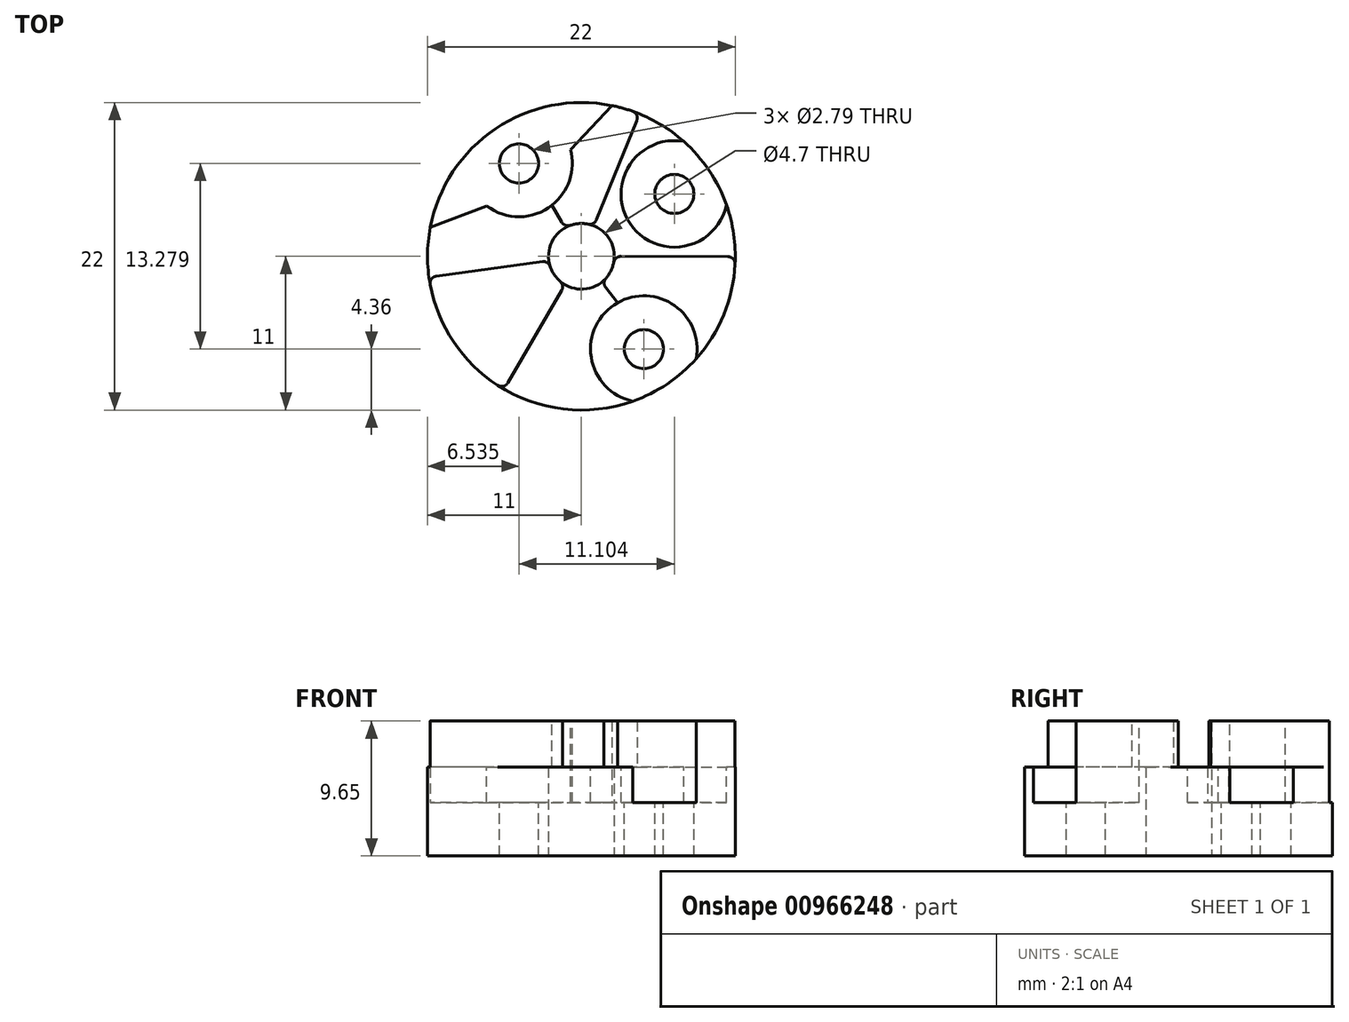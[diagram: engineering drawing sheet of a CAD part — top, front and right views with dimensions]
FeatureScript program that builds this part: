
annotation { "Feature Type Name" : "Feature", "Feature Type Description" : "" }
export const myFeature = defineFeature(function(context is Context, id is Id, definition is map)
    precondition{}
    {
        {
            var Q0;
            Q0=qCreatedBy(makeId("Top.planeOp"),FACE);
            var sketch = newSketch(context, id + "F0", { "sketchPlane" : qUnion([Q0])});
            skCircle(sketch, "E0", {"center": v(0, 0) * mm, "radius": 11 * mm});
            skCircle(sketch, "E1", {"center": v(0, 0) * mm, "radius": 2.35 * mm});
            skLineSegment(sketch, "E2", {"start": v(0, 0) * mm, "end": v(4.15, 10.19) * mm});
            skLineSegment(sketch, "E3", {"start": v(0, 0) * mm, "end": v(-5.47, 9.54) * mm});
            skLineSegment(sketch, "E4.1.0", {"start": v(0, 0) * mm, "end": v(11, -0.03) * mm});
            skLineSegment(sketch, "E4.1.1", {"start": v(0, 0) * mm, "end": v(6.75, -8.69) * mm});
            skLineSegment(sketch, "E4.2.0", {"start": v(0, 0) * mm, "end": v(-5.53, -9.5) * mm});
            skLineSegment(sketch, "E4.2.1", {"start": v(0, 0) * mm, "end": v(-10.9, -1.5) * mm});
            skLineSegment(sketch, "E4.anchor1", {"start": v(0, 0) * mm, "end": v(-5.47, 9.54) * mm, "construction": true});
            skLineSegment(sketch, "E4.anchor2", {"start": v(0, 0) * mm, "end": v(-5.53, -9.5) * mm, "construction": true});
            skSolve(sketch);
        }
        {
            var Q0;
            {var subQ0=sQuery(id+"F0.wireOp",EDGE,"E2");var subQ1=sQuery(id+"F0.wireOp",EDGE,"E0");var subQ2=makeQuery(id+"F0.imprint","INTERSECT",VERTEX,{"derivedFrom":[subQ1,subQ0]});Q0=makeQuery(id+"F0.imprint","IMPRINT",FACE,{"disambiguationData":[TD([[makeQuery(id+"F0.imprint","IMPRINT",EDGE,{"disambiguationData":[TD([[subQ2,-1.0]])],"derivedFrom":subQ1}),1.0]])]});}
            var Q1;
            {var subQ0=sQuery(id+"F0.wireOp",EDGE,"E4.2.0");var subQ1=sQuery(id+"F0.wireOp",EDGE,"E0");var subQ2=makeQuery(id+"F0.imprint","INTERSECT",VERTEX,{"derivedFrom":[subQ1,subQ0]});Q1=makeQuery(id+"F0.imprint","IMPRINT",FACE,{"disambiguationData":[TD([[makeQuery(id+"F0.imprint","IMPRINT",EDGE,{"disambiguationData":[TD([[subQ2,1.0]])],"derivedFrom":subQ1}),1.0]])]});}
            var Q2;
            {var subQ0=sQuery(id+"F0.wireOp",EDGE,"E4.1.0");var subQ1=sQuery(id+"F0.wireOp",EDGE,"E0");var subQ2=makeQuery(id+"F0.imprint","INTERSECT",VERTEX,{"derivedFrom":[subQ1,subQ0]});Q2=makeQuery(id+"F0.imprint","IMPRINT",FACE,{"disambiguationData":[TD([[makeQuery(id+"F0.imprint","IMPRINT",EDGE,{"disambiguationData":[TD([[subQ2,1.0]])],"derivedFrom":subQ1}),1.0]])]});}
            extrude(context, id + "F1", {"entities" : qUnion([Q0, Q1, Q2]), "depth" : 3.3 * mm});
        }
        {
            var Q0;
            {var subQ0=sQuery(id+"F0.wireOp",EDGE,"33BuIZ9v-IkX0-KjEr-VNsg-VApjckLjgjfI");var subQ1=sQuery(id+"F0.wireOp",EDGE,"E0");var subQ2=makeQuery(id+"F0.imprint","INTERSECT",VERTEX,{"derivedFrom":[subQ1,subQ0]});Q0=makeQuery(id+"F0.imprint","IMPRINT",FACE,{"disambiguationData":[TD([[makeQuery(id+"F0.imprint","IMPRINT",EDGE,{"disambiguationData":[TD([[subQ2,1.0]])],"derivedFrom":subQ1}),1.0]])]});}
            var Q1;
            {var subQ0=sQuery(id+"F0.wireOp",EDGE,"dZoegOkE-iBWH-g3UK-yCjy-q1fHpqfjE5M4");var subQ1=sQuery(id+"F0.wireOp",EDGE,"E0");var subQ2=makeQuery(id+"F0.imprint","INTERSECT",VERTEX,{"derivedFrom":[subQ1,subQ0]});Q1=makeQuery(id+"F0.imprint","IMPRINT",FACE,{"disambiguationData":[TD([[makeQuery(id+"F0.imprint","IMPRINT",EDGE,{"disambiguationData":[TD([[subQ2,1.0]])],"derivedFrom":subQ1}),1.0]])]});}
            var Q2;
            {var subQ0=sQuery(id+"F0.wireOp",EDGE,"073fcc1c-5e5f-4306-95f4-ba863140295b.1.1");var subQ1=sQuery(id+"F0.wireOp",EDGE,"E0");var subQ2=makeQuery(id+"F0.imprint","INTERSECT",VERTEX,{"derivedFrom":[subQ1,subQ0]});Q2=makeQuery(id+"F0.imprint","IMPRINT",FACE,{"disambiguationData":[TD([[makeQuery(id+"F0.imprint","IMPRINT",EDGE,{"disambiguationData":[TD([[subQ2,1.0]])],"derivedFrom":subQ1}),1.0]])]});}
            var Q3;
            {var subQ0=sQuery(id+"F0.wireOp",EDGE,"073fcc1c-5e5f-4306-95f4-ba863140295b.1.0");var subQ1=sQuery(id+"F0.wireOp",EDGE,"E0");var subQ2=makeQuery(id+"F0.imprint","INTERSECT",VERTEX,{"derivedFrom":[subQ1,subQ0]});Q3=makeQuery(id+"F0.imprint","IMPRINT",FACE,{"disambiguationData":[TD([[makeQuery(id+"F0.imprint","IMPRINT",EDGE,{"disambiguationData":[TD([[subQ2,1.0]])],"derivedFrom":subQ1}),1.0]])]});}
            var Q4;
            {var subQ0=sQuery(id+"F0.wireOp",EDGE,"073fcc1c-5e5f-4306-95f4-ba863140295b.2.0");var subQ1=sQuery(id+"F0.wireOp",EDGE,"E0");var subQ2=makeQuery(id+"F0.imprint","INTERSECT",VERTEX,{"derivedFrom":[subQ1,subQ0]});Q4=makeQuery(id+"F0.imprint","IMPRINT",FACE,{"disambiguationData":[TD([[makeQuery(id+"F0.imprint","IMPRINT",EDGE,{"disambiguationData":[TD([[subQ2,1.0]])],"derivedFrom":subQ1}),1.0]])]});}
            var Q5;
            {var subQ0=sQuery(id+"F0.wireOp",EDGE,"33BuIZ9v-IkX0-KjEr-VNsg-VApjckLjgjfI");var subQ1=sQuery(id+"F0.wireOp",EDGE,"E0");var subQ2=makeQuery(id+"F0.imprint","INTERSECT",VERTEX,{"derivedFrom":[subQ1,subQ0]});Q5=makeQuery(id+"F0.imprint","IMPRINT",FACE,{"disambiguationData":[TD([[makeQuery(id+"F0.imprint","IMPRINT",EDGE,{"disambiguationData":[TD([[subQ2,-1.0]])],"derivedFrom":subQ1}),1.0]])]});}
            extrude(context, id + "F2", {"entities" : qUnion([Q0, Q1, Q2, Q3, Q4, Q5]), "operationType" : NewBodyOperationType.ADD, "oppositeDirection" : true, "depth" : 6.35 * mm});
        }
        {
            var Q0;
            Q0=makeQuery(id+"F1.opExtrude","SWEPT_EDGE",EDGE,{"disambiguationData":[OSD([sQuery(id+"F0.wireOp",EDGE,"E0"),sQuery(id+"F0.wireOp",EDGE,"E2")])]});
            var Q1;
            Q1=makeQuery(id+"F1.opExtrude","SWEPT_EDGE",EDGE,{"disambiguationData":[OSD([sQuery(id+"F0.wireOp",EDGE,"E0"),sQuery(id+"F0.wireOp",EDGE,"E4.1.0")])]});
            var Q2;
            Q2=makeQuery(id+"F1.opExtrude","SWEPT_EDGE",EDGE,{"disambiguationData":[OSD([sQuery(id+"F0.wireOp",EDGE,"E0"),sQuery(id+"F0.wireOp",EDGE,"E3")])]});
            var Q3;
            Q3=makeQuery(id+"F1.opExtrude","SWEPT_EDGE",EDGE,{"disambiguationData":[OSD([sQuery(id+"F0.wireOp",EDGE,"E0"),sQuery(id+"F0.wireOp",EDGE,"E4.1.1")])]});
            var Q4;
            Q4=makeQuery(id+"F1.opExtrude","SWEPT_EDGE",EDGE,{"disambiguationData":[OSD([sQuery(id+"F0.wireOp",EDGE,"E0"),sQuery(id+"F0.wireOp",EDGE,"E4.2.0")])]});
            var Q5;
            Q5=makeQuery(id+"F1.opExtrude","SWEPT_EDGE",EDGE,{"disambiguationData":[OSD([sQuery(id+"F0.wireOp",EDGE,"E0"),sQuery(id+"F0.wireOp",EDGE,"E4.2.1")])]});
            fillet(context, id + "F3", {"entities" : qUnion([Q0, Q1, Q2, Q3, Q4, Q5]), "radius" : 0.5 * mm, "tangentPropagation" : true, "allowEdgeOverflow" : false});
        }
        {
            var Q0;
            Q0=makeQuery(id+"F1.opExtrude","SWEPT_EDGE",EDGE,{"disambiguationData":[OSD([sQuery(id+"F0.wireOp",EDGE,"E1"),sQuery(id+"F0.wireOp",EDGE,"E4.2.1")])]});
            var Q1;
            Q1=makeQuery(id+"F1.opExtrude","SWEPT_EDGE",EDGE,{"disambiguationData":[OSD([sQuery(id+"F0.wireOp",EDGE,"E1"),sQuery(id+"F0.wireOp",EDGE,"E4.2.0")])]});
            var Q2;
            Q2=makeQuery(id+"F1.opExtrude","SWEPT_EDGE",EDGE,{"disambiguationData":[OSD([sQuery(id+"F0.wireOp",EDGE,"E1"),sQuery(id+"F0.wireOp",EDGE,"E3")])]});
            var Q3;
            Q3=makeQuery(id+"F1.opExtrude","SWEPT_EDGE",EDGE,{"disambiguationData":[OSD([sQuery(id+"F0.wireOp",EDGE,"E1"),sQuery(id+"F0.wireOp",EDGE,"E2")])]});
            var Q4;
            Q4=makeQuery(id+"F1.opExtrude","SWEPT_EDGE",EDGE,{"disambiguationData":[OSD([sQuery(id+"F0.wireOp",EDGE,"E1"),sQuery(id+"F0.wireOp",EDGE,"E4.1.1")])]});
            var Q5;
            Q5=makeQuery(id+"F1.opExtrude","SWEPT_EDGE",EDGE,{"disambiguationData":[OSD([sQuery(id+"F0.wireOp",EDGE,"E1"),sQuery(id+"F0.wireOp",EDGE,"E4.1.0")])]});
            fillet(context, id + "F4", {"entities" : qUnion([Q0, Q1, Q2, Q3, Q4, Q5]), "radius" : 0.5 * mm, "tangentPropagation" : true, "allowEdgeOverflow" : false});
        }
        {
            var Q0;
            {var subQ1=sQuery(id+"F0.wireOp",EDGE,"E0");var subQ4=sQuery(id+"F0.wireOp",EDGE,"E1");var subQ5=sQuery(id+"F0.wireOp",EDGE,"E2");Q0=makeQuery(id+"F2.boolean.opBoolean","SPLIT",FACE,{"disambiguationData":[TD([makeQuery(id+"F1.opExtrude","SWEPT_FACE",FACE,{"disambiguationData":[OSD([subQ5])]})])],"derivedFrom":makeQuery(id+"F2.opExtrude","CAP_FACE",FACE,{"disambiguationData":[OSD([subQ1,subQ4])],"isStart":true})});}
            var sketch = newSketch(context, id + "F5", { "sketchPlane" : qUnion([Q0])});
            skCircle(sketch, "E5", {"center": v(6.64, 4.46) * mm, "radius": 1.4 * mm});
            skCircle(sketch, "E6.1.0", {"center": v(-4.46, 6.64) * mm, "radius": 1.4 * mm});
            skCircle(sketch, "E6.2.0", {"center": v(-6.64, -4.46) * mm, "radius": 1.4 * mm});
            skCircle(sketch, "E6.3.0", {"center": v(4.46, -6.64) * mm, "radius": 1.4 * mm});
            skPoint(sketch, "E6.center", {"position": v(0, 0) * mm});
            skSolve(sketch);
        }
        {
            var Q0;
            Q0=makeQuery(id+"F5.imprint","IMPRINT",FACE,{"disambiguationData":[TD([[makeQuery(id+"F5.imprint","IMPRINT",EDGE,{"derivedFrom":sQuery(id+"F5.wireOp",EDGE,"E6.1.0")}),1.0]])]});
            var Q1;
            Q1=makeQuery(id+"F5.imprint","IMPRINT",FACE,{"disambiguationData":[TD([[makeQuery(id+"F5.imprint","IMPRINT",EDGE,{"derivedFrom":sQuery(id+"F5.wireOp",EDGE,"E5")}),1.0]])]});
            var Q2;
            Q2=makeQuery(id+"F5.imprint","IMPRINT",FACE,{"disambiguationData":[TD([[makeQuery(id+"F5.imprint","IMPRINT",EDGE,{"derivedFrom":sQuery(id+"F5.wireOp",EDGE,"E6.3.0")}),1.0]])]});
            extrude(context, id + "F6", {"entities" : qUnion([Q0, Q1, Q2]), "operationType" : NewBodyOperationType.REMOVE, "endBound" : BoundingType.THROUGH_ALL, "oppositeDirection" : true, "depth" : 25.4 * mm, "hasSecondDirection" : true, "secondDirectionOppositeDirection" : false, "secondDirectionDepth" : 25.4 * mm});
        }
        {
            var Q0;
            Q0=makeQuery(id+"F1.opExtrude","CAP_FACE",FACE,{"disambiguationData":[OSD([sQuery(id+"F0.wireOp",EDGE,"E0"),sQuery(id+"F0.wireOp",EDGE,"E1"),sQuery(id+"F0.wireOp",EDGE,"E2"),sQuery(id+"F0.wireOp",EDGE,"E3")])],"isStart":false});
            var sketch = newSketch(context, id + "F7", { "sketchPlane" : qUnion([Q0])});
            skCircle(sketch, "E7", {"center": v(-4.46, 6.64) * mm, "radius": 3.8 * mm});
            skCircle(sketch, "E8.1.0", {"center": v(-6.64, -4.46) * mm, "radius": 3.8 * mm});
            skCircle(sketch, "E8.2.0", {"center": v(4.46, -6.64) * mm, "radius": 3.8 * mm});
            skCircle(sketch, "E8.3.0", {"center": v(6.64, 4.46) * mm, "radius": 3.8 * mm});
            skPoint(sketch, "E8.center", {"position": v(0, 0) * mm});
            skSolve(sketch);
        }
        {
            var Q0;
            Q0=makeQuery(id+"F7.imprint","IMPRINT",FACE,{"disambiguationData":[TD([[makeQuery(id+"F7.imprint","IMPRINT",EDGE,{"derivedFrom":sQuery(id+"F7.wireOp",EDGE,"E8.2.0")}),1.0]])]});
            var Q1;
            Q1=makeQuery(id+"F7.imprint","IMPRINT",FACE,{"disambiguationData":[TD([[makeQuery(id+"F7.imprint","IMPRINT",EDGE,{"derivedFrom":sQuery(id+"F7.wireOp",EDGE,"E8.3.0")}),1.0]])]});
            var Q2;
            {var subQ0=sQuery(id+"F0.wireOp",EDGE,"E3");var subQ1=sQuery(id+"F0.wireOp",EDGE,"E2");var subQ2=sQuery(id+"F0.wireOp",EDGE,"E1");var subQ3=sQuery(id+"F0.wireOp",EDGE,"E0");var subQ4=makeQuery(id+"F1.opExtrude","CAP_FACE",FACE,{"disambiguationData":[OSD([subQ3,subQ2,subQ1,subQ0])],"isStart":false});var subQ5=makeQuery(id+"F6.opExtrude","SWEPT_FACE",FACE,{"disambiguationData":[OSD([sQuery(id+"F5.wireOp",EDGE,"E6.1.0")])]});var subQ8=makeQuery(id+"F6.boolean.opBoolean","INTERSECT",EDGE,{"derivedFrom":[subQ4,subQ5]});Q2=makeQuery(id+"F7.imprint","IMPRINT",FACE,{"disambiguationData":[TD([[makeQuery(id+"F7.imprint","IMPRINT",EDGE,{"derivedFrom":subQ8}),1.0]])]});}
            var Q3;
            {var subQ0=sQuery(id+"F0.wireOp",EDGE,"E3");var subQ1=sQuery(id+"F0.wireOp",EDGE,"E2");var subQ2=sQuery(id+"F0.wireOp",EDGE,"E1");var subQ3=sQuery(id+"F0.wireOp",EDGE,"E0");var subQ4=makeQuery(id+"F1.opExtrude","CAP_FACE",FACE,{"disambiguationData":[OSD([subQ3,subQ2,subQ1,subQ0])],"isStart":false});var subQ5=makeQuery(id+"F6.opExtrude","SWEPT_FACE",FACE,{"disambiguationData":[OSD([sQuery(id+"F5.wireOp",EDGE,"E6.1.0")])]});var subQ8=makeQuery(id+"F6.boolean.opBoolean","INTERSECT",EDGE,{"derivedFrom":[subQ4,subQ5]});Q3=makeQuery(id+"F7.imprint","IMPRINT",FACE,{"disambiguationData":[TD([[makeQuery(id+"F7.imprint","IMPRINT",EDGE,{"derivedFrom":subQ8}),-1.0]])]});}
            extrude(context, id + "F8", {"entities" : qUnion([Q0, Q1, Q2, Q3]), "operationType" : NewBodyOperationType.REMOVE, "oppositeDirection" : true, "depth" : 5.84 * mm});
        }
        {
            var Q0;
            {var subQ0=sQuery(id+"F0.wireOp",EDGE,"E0");Q0=makeQuery(id+"F8.boolean.opBoolean","INTERSECT",EDGE,{"disambiguationData":[OD(0.0)],"derivedFrom":[makeQuery(id+"F2.boolean.opBoolean","MERGE",FACE,{"derivedFrom":[makeQuery(id+"F1.opExtrude","SWEPT_FACE",FACE,{"disambiguationData":[OSD([subQ0]),TDD([makeQuery(id+"F0.imprint","IMPRINT",EDGE,{"disambiguationData":[TD([[makeQuery(id+"F0.imprint","INTERSECT",VERTEX,{"derivedFrom":[subQ0,sQuery(id+"F0.wireOp",EDGE,"E2")]}),-1.0]])],"derivedFrom":subQ0})])]}),makeQuery(id+"F1.opExtrude","SWEPT_FACE",FACE,{"disambiguationData":[OSD([subQ0]),TDD([makeQuery(id+"F0.imprint","IMPRINT",EDGE,{"disambiguationData":[TD([[makeQuery(id+"F0.imprint","INTERSECT",VERTEX,{"derivedFrom":[subQ0,sQuery(id+"F0.wireOp",EDGE,"E4.2.0")]}),1.0]])],"derivedFrom":subQ0})])]}),makeQuery(id+"F1.opExtrude","SWEPT_FACE",FACE,{"disambiguationData":[OSD([subQ0]),TDD([makeQuery(id+"F0.imprint","IMPRINT",EDGE,{"disambiguationData":[TD([[makeQuery(id+"F0.imprint","INTERSECT",VERTEX,{"derivedFrom":[subQ0,sQuery(id+"F0.wireOp",EDGE,"E4.1.0")]}),1.0]])],"derivedFrom":subQ0})])]}),makeQuery(id+"F2.opExtrude","SWEPT_FACE",FACE,{"disambiguationData":[OSD([subQ0])]})]}),makeQuery(id+"F8.opExtrude","SWEPT_FACE",FACE,{"disambiguationData":[OSD([sQuery(id+"F7.wireOp",EDGE,"E7")])]})]});}
            chamfer(context, id + "F9", {"entities" : qUnion([Q0]), "width" : 2.54 * mm, "tangentPropagation" : true});
        }
    });
